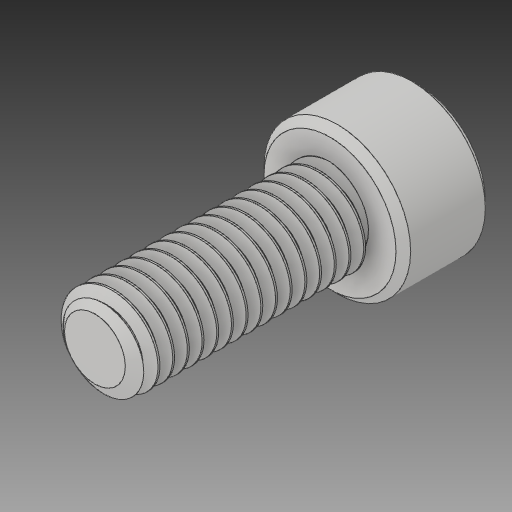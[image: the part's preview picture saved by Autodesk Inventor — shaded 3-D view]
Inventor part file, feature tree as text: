
AUTODESK INVENTOR PART (.ipt)
format: ipt  version: 2017.1 (Build 211199000, 199)  size: 818,176 bytes
history: native  units: in
note: dims shown in document units (in); Inventor stores cm internally (conversion verified against a paired STEP export)
features: chamfer x1
ambient origin geometry x8: Origin, YZ Plane, XZ Plane, XY Plane, X Axis, Y Axis, Z Axis, Center Point
bodies: Solid1 (feature_tree)
feature tree (1):
  chamfer  "Chamfer1"  [1 undecoded]
note: 1 required parameter value undecoded (feature->parameter linkage not recoverable at this tier; creation-order binding heuristic only, values carry confidence <= 0.55)
